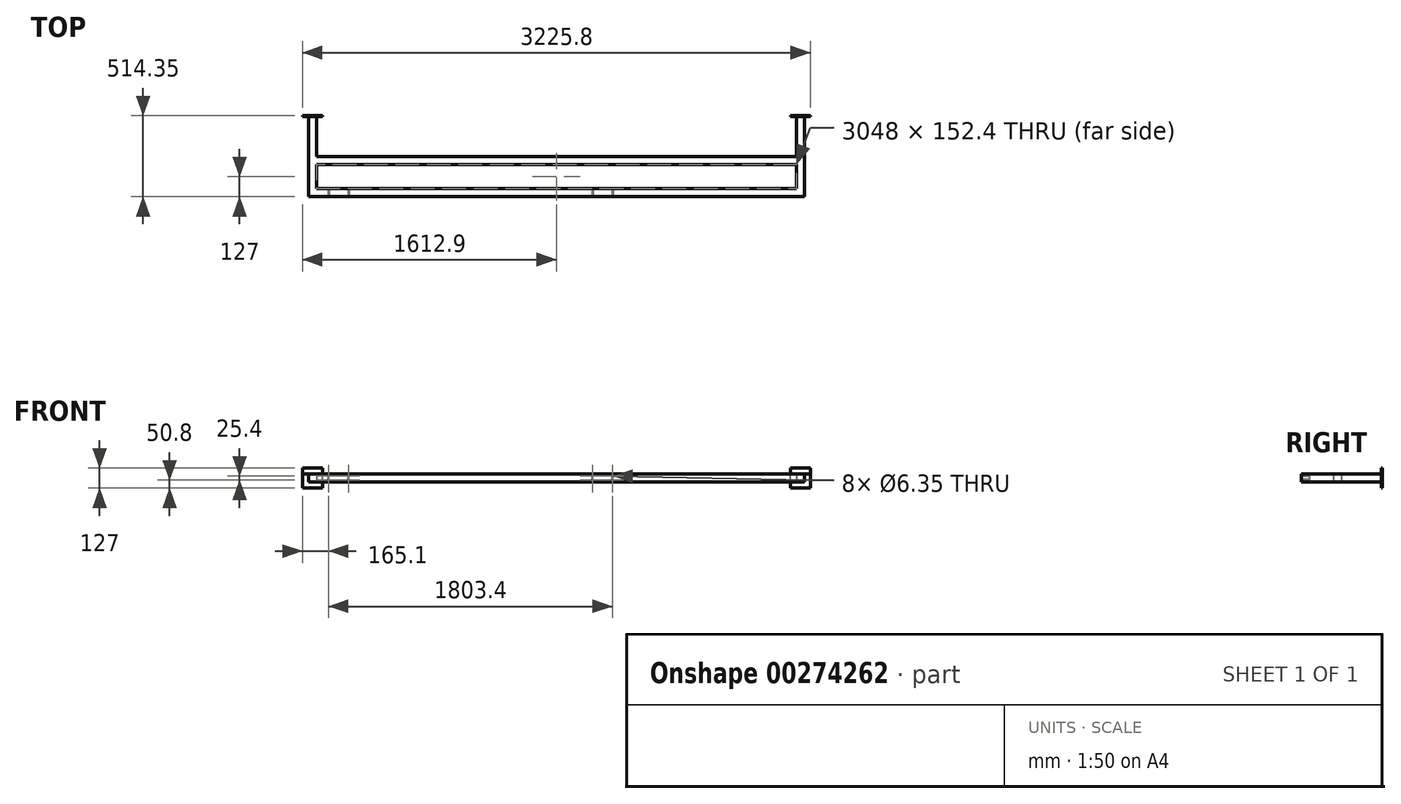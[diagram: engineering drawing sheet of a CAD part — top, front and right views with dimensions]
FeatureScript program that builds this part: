
annotation { "Feature Type Name" : "Feature", "Feature Type Description" : "" }
export const myFeature = defineFeature(function(context is Context, id is Id, definition is map)
    precondition{}
    {
        {
            var Q0;
            Q0=qCreatedBy(makeId("Front.planeOp"),FACE);
            var sketch = newSketch(context, id + "F0", { "sketchPlane" : qUnion([Q0])});
            skLineSegment(sketch, "E0.bottom", {"start": v(0, 0) * mm, "end": v(50.8, 0) * mm});
            skLineSegment(sketch, "E0.top", {"start": v(0, 50.8) * mm, "end": v(50.8, 50.8) * mm});
            skLineSegment(sketch, "E0.left", {"start": v(0, 0) * mm, "end": v(0, 50.8) * mm});
            skLineSegment(sketch, "E0.right", {"start": v(50.8, 0) * mm, "end": v(50.8, 50.8) * mm});
            skSolve(sketch);
        }
        {
            var Q0;
            Q0=makeQuery(id+"F0.imprint","IMPRINT",FACE,{"disambiguationData":[TD([[makeQuery(id+"F0.imprint","IMPRINT",EDGE,{"derivedFrom":sQuery(id+"F0.wireOp",EDGE,"E0.bottom")}),1.0]])]});
            extrude(context, id + "F1", {"entities" : qUnion([Q0]), "depth" : 508 * mm});
        }
        {
            var Q0;
            Q0=makeQuery(id+"F1.opExtrude","SWEPT_FACE",FACE,{"disambiguationData":[OSD([sQuery(id+"F0.wireOp",EDGE,"E0.right")])]});
            var sketch = newSketch(context, id + "F2", { "sketchPlane" : qUnion([Q0])});
            skLineSegment(sketch, "E1.bottom", {"start": v(-508, 50.8) * mm, "end": v(-457.2, 50.8) * mm});
            skLineSegment(sketch, "E1.top", {"start": v(-508, 0) * mm, "end": v(-457.2, 0) * mm});
            skLineSegment(sketch, "E1.left", {"start": v(-508, 50.8) * mm, "end": v(-508, 0) * mm});
            skLineSegment(sketch, "E1.right", {"start": v(-457.2, 50.8) * mm, "end": v(-457.2, 0) * mm});
            skLineSegment(sketch, "E2.bottom", {"start": v(-304.8, 50.8) * mm, "end": v(-254, 50.8) * mm});
            skLineSegment(sketch, "E2.top", {"start": v(-304.8, 0) * mm, "end": v(-254, 0) * mm});
            skLineSegment(sketch, "E2.left", {"start": v(-304.8, 50.8) * mm, "end": v(-304.8, 0) * mm});
            skLineSegment(sketch, "E2.right", {"start": v(-254, 50.8) * mm, "end": v(-254, 0) * mm});
            skSolve(sketch);
        }
        {
            var Q0;
            Q0=makeQuery(id+"F2.imprint","IMPRINT",FACE,{"disambiguationData":[TD([[makeQuery(id+"F2.imprint","IMPRINT",EDGE,{"derivedFrom":sQuery(id+"F2.wireOp",EDGE,"E1.bottom")}),-1.0]])]});
            var Q1;
            Q1=makeQuery(id+"F2.imprint","IMPRINT",FACE,{"disambiguationData":[TD([[makeQuery(id+"F2.imprint","IMPRINT",EDGE,{"derivedFrom":sQuery(id+"F2.wireOp",EDGE,"E2.bottom")}),-1.0]])]});
            extrude(context, id + "F3", {"entities" : qUnion([Q0, Q1]), "operationType" : NewBodyOperationType.ADD, "depth" : 3048 * mm});
        }
        {
            var Q0;
            Q0=makeQuery(id+"F3.boolean.opBoolean","MERGE",FACE,{"derivedFrom":[makeQuery(id+"F1.opExtrude","CAP_FACE",FACE,{"disambiguationData":[OSD([sQuery(id+"F0.wireOp",EDGE,"E0.bottom"),sQuery(id+"F0.wireOp",EDGE,"E0.top"),sQuery(id+"F0.wireOp",EDGE,"E0.left"),sQuery(id+"F0.wireOp",EDGE,"E0.right")])],"isStart":false}),makeQuery(id+"F3.opExtrude","SWEPT_FACE",FACE,{"disambiguationData":[OSD([sQuery(id+"F2.wireOp",EDGE,"E1.left")])]})]});
            var sketch = newSketch(context, id + "F4", { "sketchPlane" : qUnion([Q0])});
            skLineSegment(sketch, "E3.bottom", {"start": v(3098.8, 50.8) * mm, "end": v(3149.6, 50.8) * mm});
            skLineSegment(sketch, "E3.top", {"start": v(3098.8, 0) * mm, "end": v(3149.6, 0) * mm});
            skLineSegment(sketch, "E3.left", {"start": v(3098.8, 50.8) * mm, "end": v(3098.8, 0) * mm});
            skLineSegment(sketch, "E3.right", {"start": v(3149.6, 50.8) * mm, "end": v(3149.6, 0) * mm});
            skSolve(sketch);
        }
        {
            var Q0;
            Q0=makeQuery(id+"F4.imprint","IMPRINT",FACE,{"disambiguationData":[TD([[makeQuery(id+"F4.imprint","IMPRINT",EDGE,{"derivedFrom":sQuery(id+"F4.wireOp",EDGE,"E3.bottom")}),-1.0]])]});
            extrude(context, id + "F5", {"entities" : qUnion([Q0]), "operationType" : NewBodyOperationType.ADD, "oppositeDirection" : true, "depth" : 508 * mm});
        }
        {
            var Q0;
            Q0=makeQuery(id+"F5.boolean.opBoolean","MERGE",FACE,{"derivedFrom":[makeQuery(id+"F3.boolean.opBoolean","MERGE",FACE,{"derivedFrom":[makeQuery(id+"F1.opExtrude","SWEPT_FACE",FACE,{"disambiguationData":[OSD([sQuery(id+"F0.wireOp",EDGE,"E0.top")])]}),makeQuery(id+"F3.opExtrude","SWEPT_FACE",FACE,{"disambiguationData":[OSD([sQuery(id+"F2.wireOp",EDGE,"E1.bottom")])]}),makeQuery(id+"F3.opExtrude","SWEPT_FACE",FACE,{"disambiguationData":[OSD([sQuery(id+"F2.wireOp",EDGE,"E2.bottom")])]})]}),makeQuery(id+"F5.opExtrude","SWEPT_FACE",FACE,{"disambiguationData":[OSD([sQuery(id+"F4.wireOp",EDGE,"E3.bottom")])]})]});
            var sketch = newSketch(context, id + "F6", { "sketchPlane" : qUnion([Q0])});
            skLineSegment(sketch, "E4.bottom", {"start": v(-38.1, 0) * mm, "end": v(88.9, 0) * mm});
            skLineSegment(sketch, "E4.top", {"start": v(-38.1, 6.35) * mm, "end": v(88.9, 6.35) * mm});
            skLineSegment(sketch, "E4.left", {"start": v(-38.1, 0) * mm, "end": v(-38.1, 6.35) * mm});
            skLineSegment(sketch, "E4.right", {"start": v(88.9, 0) * mm, "end": v(88.9, 6.35) * mm});
            skLineSegment(sketch, "E5.bottom", {"start": v(3060.7, 0) * mm, "end": v(3187.7, 0) * mm});
            skLineSegment(sketch, "E5.top", {"start": v(3060.7, 6.35) * mm, "end": v(3187.7, 6.35) * mm});
            skLineSegment(sketch, "E5.left", {"start": v(3060.7, 0) * mm, "end": v(3060.7, 6.35) * mm});
            skLineSegment(sketch, "E5.right", {"start": v(3187.7, 0) * mm, "end": v(3187.7, 6.35) * mm});
            skSolve(sketch);
        }
        {
            var Q0;
            Q0=makeQuery(id+"F6.imprint","IMPRINT",FACE,{"disambiguationData":[TD([[makeQuery(id+"F6.imprint","IMPRINT",EDGE,{"derivedFrom":sQuery(id+"F6.wireOp",EDGE,"E5.top")}),-1.0]])]});
            var Q1;
            Q1=makeQuery(id+"F6.imprint","IMPRINT",FACE,{"disambiguationData":[TD([[makeQuery(id+"F6.imprint","IMPRINT",EDGE,{"derivedFrom":sQuery(id+"F6.wireOp",EDGE,"E4.top")}),-1.0]])]});
            extrude(context, id + "F7", {"entities" : qUnion([Q0, Q1]), "depth" : 38.1 * mm});
        }
        {
            var Q0;
            Q0=makeQuery(id+"F7.opExtrude","CAP_FACE",FACE,{"disambiguationData":[OSD([sQuery(id+"F6.wireOp",EDGE,"E4.bottom"),sQuery(id+"F6.wireOp",EDGE,"E4.top"),sQuery(id+"F6.wireOp",EDGE,"E4.left"),sQuery(id+"F6.wireOp",EDGE,"E4.right")])],"isStart":true});
            var Q1;
            Q1=makeQuery(id+"F7.opExtrude","CAP_FACE",FACE,{"disambiguationData":[OSD([sQuery(id+"F6.wireOp",EDGE,"E5.bottom"),sQuery(id+"F6.wireOp",EDGE,"E5.top"),sQuery(id+"F6.wireOp",EDGE,"E5.left"),sQuery(id+"F6.wireOp",EDGE,"E5.right")])],"isStart":true});
            extrude(context, id + "F8", {"entities" : qUnion([Q0, Q1]), "depth" : 88.9 * mm});
        }
        {
            var Q0;
            Q0=makeQuery(id+"F5.boolean.opBoolean","MERGE",FACE,{"derivedFrom":[makeQuery(id+"F3.boolean.opBoolean","MERGE",FACE,{"derivedFrom":[makeQuery(id+"F1.opExtrude","CAP_FACE",FACE,{"disambiguationData":[OSD([sQuery(id+"F0.wireOp",EDGE,"E0.bottom"),sQuery(id+"F0.wireOp",EDGE,"E0.top"),sQuery(id+"F0.wireOp",EDGE,"E0.left"),sQuery(id+"F0.wireOp",EDGE,"E0.right")])],"isStart":false}),makeQuery(id+"F3.opExtrude","SWEPT_FACE",FACE,{"disambiguationData":[OSD([sQuery(id+"F2.wireOp",EDGE,"E1.left")])]})]}),makeQuery(id+"F5.opExtrude","CAP_FACE",FACE,{"disambiguationData":[OSD([sQuery(id+"F4.wireOp",EDGE,"E3.bottom"),sQuery(id+"F4.wireOp",EDGE,"E3.top"),sQuery(id+"F4.wireOp",EDGE,"E3.left"),sQuery(id+"F4.wireOp",EDGE,"E3.right")])],"isStart":true})]});
            var sketch = newSketch(context, id + "F9", { "sketchPlane" : qUnion([Q0])});
            skPoint(sketch, "E6", {"position": v(127, 38.1) * mm});
            skPoint(sketch, "E7", {"position": v(127, 12.7) * mm});
            skPoint(sketch, "E8", {"position": v(254, 12.7) * mm});
            skPoint(sketch, "E9", {"position": v(254, 38.1) * mm});
            skPoint(sketch, "E10", {"position": v(1803.4, 38.1) * mm});
            skPoint(sketch, "E11", {"position": v(1803.4, 12.7) * mm});
            skPoint(sketch, "E12", {"position": v(1930.4, 38.1) * mm});
            skPoint(sketch, "E13", {"position": v(1930.4, 12.7) * mm});
            skSolve(sketch);
        }
        {
            var Q0;
            Q0=sQuery(id+"F9.wireOp",VERTEX,"E6");
            var Q1;
            Q1=sQuery(id+"F9.wireOp",VERTEX,"E9");
            var Q2;
            Q2=sQuery(id+"F9.wireOp",VERTEX,"E7");
            var Q3;
            Q3=sQuery(id+"F9.wireOp",VERTEX,"E8");
            var Q4;
            Q4=sQuery(id+"F9.wireOp",VERTEX,"E10");
            var Q5;
            Q5=sQuery(id+"F9.wireOp",VERTEX,"E11");
            var Q6;
            Q6=sQuery(id+"F9.wireOp",VERTEX,"E12");
            var Q7;
            Q7=sQuery(id+"F9.wireOp",VERTEX,"E13");
            var Q8;
            Q8=makeQuery(id+"F1.opExtrude","SWEPT_BODY",BODY,{"disambiguationData":[OSD([sQuery(id+"F0.wireOp",EDGE,"E0.bottom"),sQuery(id+"F0.wireOp",EDGE,"E0.top"),sQuery(id+"F0.wireOp",EDGE,"E0.left"),sQuery(id+"F0.wireOp",EDGE,"E0.right")])]});
            hole(context, id + "F10", {"style" : HoleStyle.SIMPLE, "endStyle" : HoleEndStyle.BLIND, "holeDiameter" : 6.35 * mm, "holeDepth" : 50.8 * mm, "tappedDepth" : 12.7 * mm, "tapClearance" : 3, "locations" : qUnion([Q0, Q1, Q2, Q3, Q4, Q5, Q6, Q7]), "scope" : qUnion([Q8])});
        }
    });
